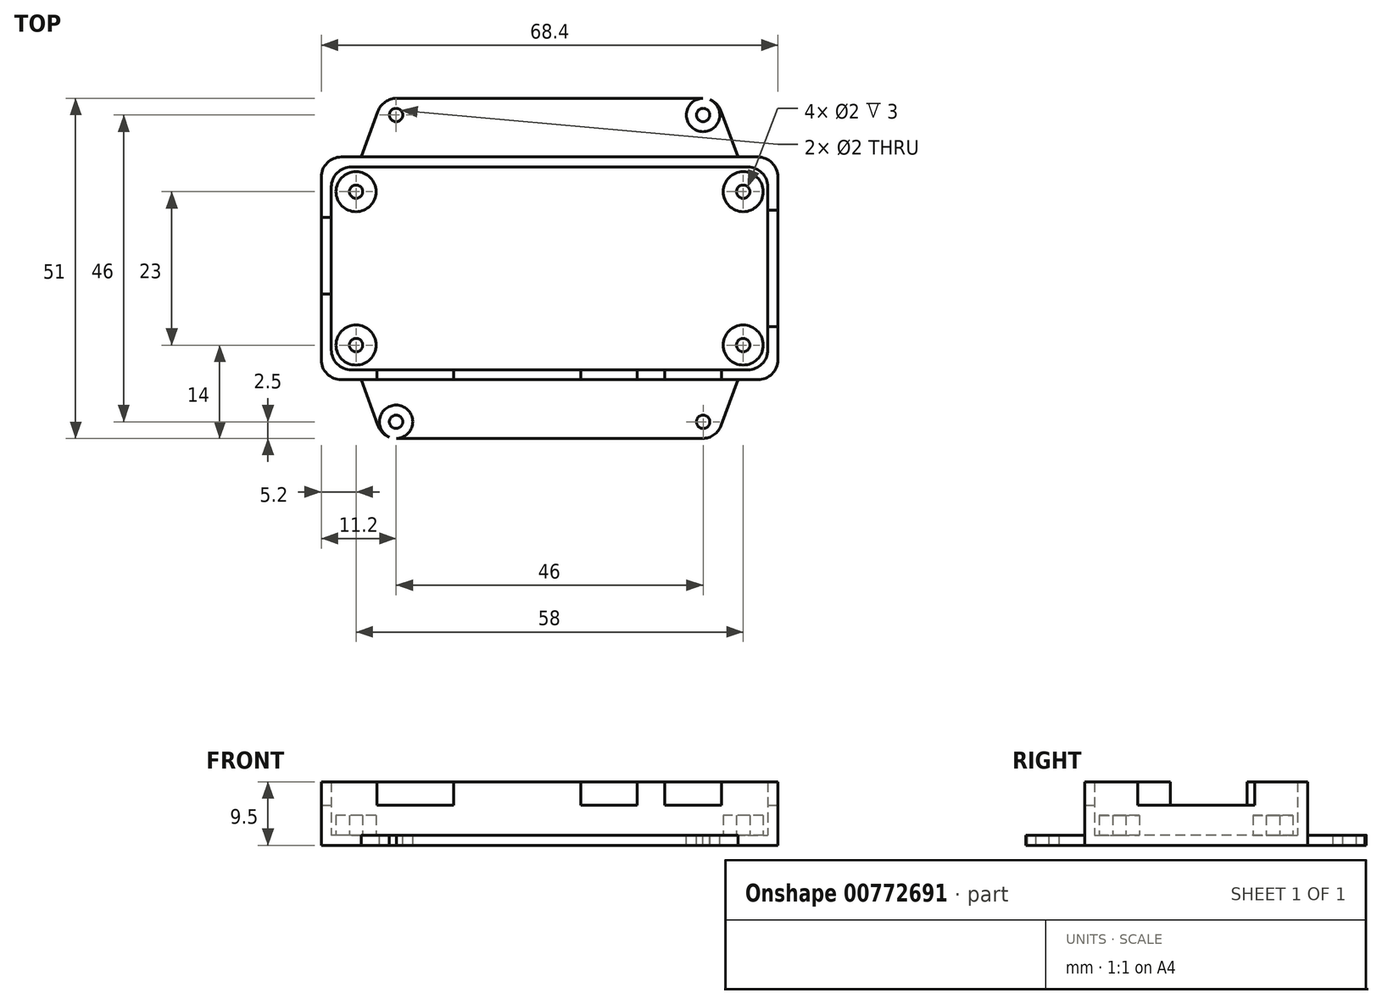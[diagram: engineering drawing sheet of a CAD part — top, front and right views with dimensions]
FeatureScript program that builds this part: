
annotation { "Feature Type Name" : "Feature", "Feature Type Description" : "" }
export const myFeature = defineFeature(function(context is Context, id is Id, definition is map)
    precondition{}
    {
        {
            var Q0;
            Q0=qCreatedBy(makeId("Top.planeOp"),FACE);
            var sketch = newSketch(context, id + "F0", { "sketchPlane" : qUnion([Q0])});
            skLineSegment(sketch, "E0", {"start": v(0, 31.79) * mm, "end": v(0, -34.92) * mm, "construction": true});
            skLineSegment(sketch, "E1", {"start": v(-57.68, 0) * mm, "end": v(57.82, 0) * mm, "construction": true});
            skLineSegment(sketch, "E2.bottom", {"start": v(-29.5, 15) * mm, "end": v(29.5, 15) * mm, "construction": true});
            skLineSegment(sketch, "E2.top", {"start": v(-29.5, -15) * mm, "end": v(29.5, -15) * mm, "construction": true});
            skLineSegment(sketch, "E2.left", {"start": v(-32.5, 12) * mm, "end": v(-32.5, -12) * mm, "construction": true});
            skLineSegment(sketch, "E2.right", {"start": v(32.5, 12) * mm, "end": v(32.5, -12) * mm, "construction": true});
            skPoint(sketch, "E3.visualSharp", {"position": v(-32.5, 15) * mm});
            skArc(sketch, "E3.filletArc", {"start": v(-29.5, 15) * mm, "mid": v(-31.62, 14.12) * mm, "end": v(-32.5, 12) * mm, "construction": true});
            skPoint(sketch, "E4.visualSharp", {"position": v(32.5, 15) * mm});
            skArc(sketch, "E4.filletArc", {"start": v(32.5, 12) * mm, "mid": v(31.62, 14.12) * mm, "end": v(29.5, 15) * mm, "construction": true});
            skPoint(sketch, "E5.visualSharp", {"position": v(32.5, -15) * mm});
            skArc(sketch, "E5.filletArc", {"start": v(29.5, -15) * mm, "mid": v(31.62, -14.12) * mm, "end": v(32.5, -12) * mm, "construction": true});
            skPoint(sketch, "E6.visualSharp", {"position": v(-32.5, -15) * mm});
            skArc(sketch, "E6.filletArc", {"start": v(-32.5, -12) * mm, "mid": v(-31.62, -14.12) * mm, "end": v(-29.5, -15) * mm, "construction": true});
            skCircle(sketch, "E7", {"center": v(-29, 11.5) * mm, "radius": 3 * mm});
            skCircle(sketch, "E8.0.1.0", {"center": v(-29, -11.5) * mm, "radius": 3 * mm});
            skCircle(sketch, "E8.1.0.0", {"center": v(29, 11.5) * mm, "radius": 3 * mm});
            skCircle(sketch, "E8.1.1.0", {"center": v(29, -11.5) * mm, "radius": 3 * mm});
            skLineSegment(sketch, "E8.direction1", {"start": v(-29, 11.5) * mm, "end": v(29, 11.5) * mm, "construction": true});
            skLineSegment(sketch, "E8.direction2", {"start": v(-29, 11.5) * mm, "end": v(-29, -11.5) * mm, "construction": true});
            skCircle(sketch, "E9", {"center": v(-29, 11.5) * mm, "radius": 1 * mm});
            skCircle(sketch, "E10.0.1.0", {"center": v(-29, -11.5) * mm, "radius": 1 * mm});
            skCircle(sketch, "E10.1.0.0", {"center": v(29, 11.5) * mm, "radius": 1 * mm});
            skCircle(sketch, "E10.1.1.0", {"center": v(29, -11.5) * mm, "radius": 1 * mm});
            skLineSegment(sketch, "E11.bottom", {"start": v(-29.7, 15.2) * mm, "end": v(29.7, 15.2) * mm});
            skLineSegment(sketch, "E11.top", {"start": v(-29.7, -15.2) * mm, "end": v(29.7, -15.2) * mm});
            skLineSegment(sketch, "E11.left", {"start": v(-32.7, 12.2) * mm, "end": v(-32.7, -12.2) * mm});
            skLineSegment(sketch, "E11.right", {"start": v(32.7, 12.2) * mm, "end": v(32.7, -12.2) * mm});
            skPoint(sketch, "E12.visualSharp", {"position": v(-32.7, 15.2) * mm});
            skArc(sketch, "E12.filletArc", {"start": v(-29.7, 15.2) * mm, "mid": v(-31.82, 14.32) * mm, "end": v(-32.7, 12.2) * mm});
            skPoint(sketch, "E13.visualSharp", {"position": v(-32.7, -15.2) * mm});
            skArc(sketch, "E13.filletArc", {"start": v(-32.7, -12.2) * mm, "mid": v(-31.82, -14.32) * mm, "end": v(-29.7, -15.2) * mm});
            skPoint(sketch, "E14.visualSharp", {"position": v(32.7, -15.2) * mm});
            skArc(sketch, "E14.filletArc", {"start": v(29.7, -15.2) * mm, "mid": v(31.82, -14.32) * mm, "end": v(32.7, -12.2) * mm});
            skPoint(sketch, "E15.visualSharp", {"position": v(32.7, 15.2) * mm});
            skArc(sketch, "E15.filletArc", {"start": v(32.7, 12.2) * mm, "mid": v(31.82, 14.32) * mm, "end": v(29.7, 15.2) * mm});
            skLineSegment(sketch, "E16.bottom", {"start": v(-31.2, 16.7) * mm, "end": v(31.2, 16.7) * mm});
            skLineSegment(sketch, "E16.top", {"start": v(-31.2, -16.7) * mm, "end": v(31.2, -16.7) * mm});
            skLineSegment(sketch, "E16.left", {"start": v(-34.2, 13.7) * mm, "end": v(-34.2, -13.7) * mm});
            skLineSegment(sketch, "E16.right", {"start": v(34.2, 13.7) * mm, "end": v(34.2, -13.7) * mm});
            skPoint(sketch, "E17.visualSharp", {"position": v(-34.2, 16.7) * mm});
            skArc(sketch, "E17.filletArc", {"start": v(-31.2, 16.7) * mm, "mid": v(-33.32, 15.82) * mm, "end": v(-34.2, 13.7) * mm});
            skPoint(sketch, "E18.visualSharp", {"position": v(-34.2, -16.7) * mm});
            skArc(sketch, "E18.filletArc", {"start": v(-34.2, -13.7) * mm, "mid": v(-33.32, -15.82) * mm, "end": v(-31.2, -16.7) * mm});
            skPoint(sketch, "E19.visualSharp", {"position": v(34.2, -16.7) * mm});
            skArc(sketch, "E19.filletArc", {"start": v(31.2, -16.7) * mm, "mid": v(33.32, -15.82) * mm, "end": v(34.2, -13.7) * mm});
            skPoint(sketch, "E20.visualSharp", {"position": v(34.2, 16.7) * mm});
            skArc(sketch, "E20.filletArc", {"start": v(34.2, 13.7) * mm, "mid": v(33.32, 15.82) * mm, "end": v(31.2, 16.7) * mm});
            skLineSegment(sketch, "E21", {"start": v(-36.24, 1.9) * mm, "end": v(-30.97, 1.9) * mm, "construction": true});
            skLineSegment(sketch, "E22", {"start": v(-20.1, -13.64) * mm, "end": v(-20.1, -19.07) * mm, "construction": true});
            skLineSegment(sketch, "E23", {"start": v(8.9, -12.93) * mm, "end": v(8.9, -18.66) * mm, "construction": true});
            skLineSegment(sketch, "E24", {"start": v(21.5, -12.58) * mm, "end": v(21.5, -18.71) * mm, "construction": true});
            skLineSegment(sketch, "E25", {"start": v(-25.85, -16.7) * mm, "end": v(-25.85, -15.2) * mm});
            skLineSegment(sketch, "E26", {"start": v(-14.35, -16.7) * mm, "end": v(-14.35, -15.2) * mm});
            skLineSegment(sketch, "E27", {"start": v(4.65, -16.7) * mm, "end": v(4.65, -15.2) * mm});
            skLineSegment(sketch, "E28", {"start": v(13.15, -15.2) * mm, "end": v(13.15, -16.7) * mm});
            skLineSegment(sketch, "E29", {"start": v(17.25, -16.7) * mm, "end": v(17.25, -15.2) * mm});
            skLineSegment(sketch, "E30", {"start": v(25.75, -15.2) * mm, "end": v(25.75, -16.7) * mm});
            skLineSegment(sketch, "E31", {"start": v(-34.2, 7.65) * mm, "end": v(-32.7, 7.65) * mm});
            skLineSegment(sketch, "E32", {"start": v(-34.2, -3.85) * mm, "end": v(-32.7, -3.85) * mm});
            skLineSegment(sketch, "E33", {"start": v(32.7, 8.75) * mm, "end": v(34.2, 8.75) * mm});
            skLineSegment(sketch, "E34", {"start": v(32.7, -8.75) * mm, "end": v(34.2, -8.75) * mm});
            skSolve(sketch);
        }
        {
            var Q0;
            Q0 = qSketchRegion(id + "F0", true);
            var Q1;
            Q1=makeQuery(id+"F0.imprint","IMPRINT",FACE,{"disambiguationData":[TD([[makeQuery(id+"F0.imprint","IMPRINT",EDGE,{"derivedFrom":sQuery(id+"F0.wireOp",EDGE,"E7")}),-1.0]])]});
            var Q2;
            Q2=makeQuery(id+"F0.imprint","IMPRINT",FACE,{"disambiguationData":[TD([[makeQuery(id+"F0.imprint","IMPRINT",EDGE,{"derivedFrom":sQuery(id+"F0.wireOp",EDGE,"E10.0.1.0")}),1.0]])]});
            var Q3;
            Q3=makeQuery(id+"F0.imprint","IMPRINT",FACE,{"disambiguationData":[TD([[makeQuery(id+"F0.imprint","IMPRINT",EDGE,{"derivedFrom":sQuery(id+"F0.wireOp",EDGE,"E8.0.1.0")}),1.0]])]});
            var Q4;
            Q4=makeQuery(id+"F0.imprint","IMPRINT",FACE,{"disambiguationData":[TD([[makeQuery(id+"F0.imprint","IMPRINT",EDGE,{"derivedFrom":sQuery(id+"F0.wireOp",EDGE,"E9")}),1.0]])]});
            var Q5;
            Q5=makeQuery(id+"F0.imprint","IMPRINT",FACE,{"disambiguationData":[TD([[makeQuery(id+"F0.imprint","IMPRINT",EDGE,{"derivedFrom":sQuery(id+"F0.wireOp",EDGE,"E7")}),1.0]])]});
            var Q6;
            Q6=makeQuery(id+"F0.imprint","IMPRINT",FACE,{"disambiguationData":[TD([[makeQuery(id+"F0.imprint","IMPRINT",EDGE,{"derivedFrom":sQuery(id+"F0.wireOp",EDGE,"E10.1.1.0")}),1.0]])]});
            var Q7;
            Q7=makeQuery(id+"F0.imprint","IMPRINT",FACE,{"disambiguationData":[TD([[makeQuery(id+"F0.imprint","IMPRINT",EDGE,{"derivedFrom":sQuery(id+"F0.wireOp",EDGE,"E8.1.1.0")}),1.0]])]});
            var Q8;
            Q8=makeQuery(id+"F0.imprint","IMPRINT",FACE,{"disambiguationData":[TD([[makeQuery(id+"F0.imprint","IMPRINT",EDGE,{"derivedFrom":sQuery(id+"F0.wireOp",EDGE,"E10.1.0.0")}),1.0]])]});
            var Q9;
            Q9=makeQuery(id+"F0.imprint","IMPRINT",FACE,{"disambiguationData":[TD([[makeQuery(id+"F0.imprint","IMPRINT",EDGE,{"derivedFrom":sQuery(id+"F0.wireOp",EDGE,"E8.1.0.0")}),1.0]])]});
            extrude(context, id + "F1", {"entities" : qUnion([Q0, Q1, Q2, Q3, Q4, Q5, Q6, Q7, Q8, Q9]), "oppositeDirection" : true, "depth" : 1.5 * mm, "offsetDistance" : 25 * mm});
        }
        {
            var Q0;
            Q0=makeQuery(id+"F0.imprint","IMPRINT",FACE,{"disambiguationData":[TD([[makeQuery(id+"F0.imprint","IMPRINT",EDGE,{"derivedFrom":sQuery(id+"F0.wireOp",EDGE,"E7")}),1.0]])]});
            var Q1;
            Q1=makeQuery(id+"F0.imprint","IMPRINT",FACE,{"disambiguationData":[TD([[makeQuery(id+"F0.imprint","IMPRINT",EDGE,{"derivedFrom":sQuery(id+"F0.wireOp",EDGE,"E8.0.1.0")}),1.0]])]});
            var Q2;
            Q2=makeQuery(id+"F0.imprint","IMPRINT",FACE,{"disambiguationData":[TD([[makeQuery(id+"F0.imprint","IMPRINT",EDGE,{"derivedFrom":sQuery(id+"F0.wireOp",EDGE,"E8.1.0.0")}),1.0]])]});
            var Q3;
            Q3=makeQuery(id+"F0.imprint","IMPRINT",FACE,{"disambiguationData":[TD([[makeQuery(id+"F0.imprint","IMPRINT",EDGE,{"derivedFrom":sQuery(id+"F0.wireOp",EDGE,"E8.1.1.0")}),1.0]])]});
            extrude(context, id + "F2", {"entities" : qUnion([Q0, Q1, Q2, Q3]), "operationType" : NewBodyOperationType.ADD, "depth" : 3 * mm, "offsetDistance" : 25 * mm});
        }
        {
            var Q0;
            {var subQ3=sQuery(id+"F0.wireOp",EDGE,"E13.filletArc");Q0=makeQuery(id+"F0.imprint","IMPRINT",FACE,{"disambiguationData":[TD([[makeQuery(id+"F0.imprint","IMPRINT",EDGE,{"derivedFrom":subQ3}),-1.0]])]});}
            var Q1;
            Q1=makeQuery(id+"F0.imprint","IMPRINT",FACE,{"disambiguationData":[TD([[makeQuery(id+"F0.imprint","IMPRINT",EDGE,{"derivedFrom":sQuery(id+"F0.wireOp",EDGE,"E11.bottom")}),1.0]])]});
            var Q2;
            {var subQ0=sQuery(id+"F0.wireOp",EDGE,"E26");Q2=makeQuery(id+"F0.imprint","IMPRINT",FACE,{"disambiguationData":[TD([[makeQuery(id+"F0.imprint","IMPRINT",EDGE,{"derivedFrom":subQ0}),-1.0]])]});}
            var Q3;
            {var subQ0=sQuery(id+"F0.wireOp",EDGE,"E28");Q3=makeQuery(id+"F0.imprint","IMPRINT",FACE,{"disambiguationData":[TD([[makeQuery(id+"F0.imprint","IMPRINT",EDGE,{"derivedFrom":subQ0}),1.0]])]});}
            var Q4;
            {var subQ3=sQuery(id+"F0.wireOp",EDGE,"E14.filletArc");Q4=makeQuery(id+"F0.imprint","IMPRINT",FACE,{"disambiguationData":[TD([[makeQuery(id+"F0.imprint","IMPRINT",EDGE,{"derivedFrom":subQ3}),-1.0]])]});}
            extrude(context, id + "F3", {"entities" : qUnion([Q0, Q1, Q2, Q3, Q4]), "operationType" : NewBodyOperationType.ADD, "depth" : 8 * mm, "offsetDistance" : 25 * mm});
        }
        {
            var Q0;
            {var subQ0=sQuery(id+"F0.wireOp",EDGE,"E31");Q0=makeQuery(id+"F0.imprint","IMPRINT",FACE,{"disambiguationData":[TD([[makeQuery(id+"F0.imprint","IMPRINT",EDGE,{"derivedFrom":subQ0}),-1.0]])]});}
            var Q1;
            {var subQ0=sQuery(id+"F0.wireOp",EDGE,"E25");Q1=makeQuery(id+"F0.imprint","IMPRINT",FACE,{"disambiguationData":[TD([[makeQuery(id+"F0.imprint","IMPRINT",EDGE,{"derivedFrom":subQ0}),-1.0]])]});}
            var Q2;
            {var subQ0=sQuery(id+"F0.wireOp",EDGE,"E27");Q2=makeQuery(id+"F0.imprint","IMPRINT",FACE,{"disambiguationData":[TD([[makeQuery(id+"F0.imprint","IMPRINT",EDGE,{"derivedFrom":subQ0}),-1.0]])]});}
            var Q3;
            {var subQ0=sQuery(id+"F0.wireOp",EDGE,"E29");Q3=makeQuery(id+"F0.imprint","IMPRINT",FACE,{"disambiguationData":[TD([[makeQuery(id+"F0.imprint","IMPRINT",EDGE,{"derivedFrom":subQ0}),-1.0]])]});}
            var Q4;
            {var subQ0=sQuery(id+"F0.wireOp",EDGE,"E33");Q4=makeQuery(id+"F0.imprint","IMPRINT",FACE,{"disambiguationData":[TD([[makeQuery(id+"F0.imprint","IMPRINT",EDGE,{"derivedFrom":subQ0}),-1.0]])]});}
            extrude(context, id + "F4", {"entities" : qUnion([Q0, Q1, Q2, Q3, Q4]), "operationType" : NewBodyOperationType.ADD, "depth" : 4.5 * mm, "offsetDistance" : 25 * mm});
        }
        {
            var Q0;
            Q0=qCreatedBy(makeId("Top.planeOp"),FACE);
            var sketch = newSketch(context, id + "F5", { "sketchPlane" : qUnion([Q0])});
            skLineSegment(sketch, "E35.0", {"start": v(-31.2, 16.7) * mm, "end": v(31.2, 16.7) * mm, "construction": true});
            skLineSegment(sketch, "E36", {"start": v(-28.2, 16.7) * mm, "end": v(-25.72, 23.53) * mm});
            skLineSegment(sketch, "E37", {"start": v(-22.9, 25.5) * mm, "end": v(22.9, 25.5) * mm});
            skLineSegment(sketch, "E38", {"start": v(25.72, 23.53) * mm, "end": v(28.2, 16.7) * mm});
            skLineSegment(sketch, "E39.0", {"start": v(-31.2, -16.7) * mm, "end": v(31.2, -16.7) * mm, "construction": true});
            skLineSegment(sketch, "E40", {"start": v(-28.2, -16.7) * mm, "end": v(-25.72, -23.53) * mm});
            skLineSegment(sketch, "E41", {"start": v(-22.9, -25.5) * mm, "end": v(22.9, -25.5) * mm});
            skLineSegment(sketch, "E42", {"start": v(25.72, -23.53) * mm, "end": v(28.2, -16.7) * mm});
            skPoint(sketch, "E43.visualSharp", {"position": v(-25, -25.5) * mm});
            skArc(sketch, "E43.filletArc", {"start": v(-25.72, -23.53) * mm, "mid": v(-24.62, -24.96) * mm, "end": v(-22.9, -25.5) * mm});
            skPoint(sketch, "E44.visualSharp", {"position": v(25, -25.5) * mm});
            skArc(sketch, "E44.filletArc", {"start": v(22.9, -25.5) * mm, "mid": v(24.62, -24.96) * mm, "end": v(25.72, -23.53) * mm});
            skPoint(sketch, "E45.visualSharp", {"position": v(25, 25.5) * mm});
            skArc(sketch, "E45.filletArc", {"start": v(25.72, 23.53) * mm, "mid": v(24.62, 24.96) * mm, "end": v(22.9, 25.5) * mm});
            skPoint(sketch, "E46.visualSharp", {"position": v(-25, 25.5) * mm});
            skArc(sketch, "E46.filletArc", {"start": v(-22.9, 25.5) * mm, "mid": v(-24.62, 24.96) * mm, "end": v(-25.72, 23.53) * mm});
            skLineSegment(sketch, "E47", {"start": v(-28.2, 16.7) * mm, "end": v(28.2, 16.7) * mm});
            skLineSegment(sketch, "E48", {"start": v(-28.2, -16.7) * mm, "end": v(28.2, -16.7) * mm});
            skCircle(sketch, "E49", {"center": v(-23, 23) * mm, "radius": 2.5 * mm});
            skCircle(sketch, "E50.MirrorC", {"center": v(23, 23) * mm, "radius": 2.5 * mm});
            skCircle(sketch, "E51.MirrorC", {"center": v(-23, -23) * mm, "radius": 2.5 * mm});
            skCircle(sketch, "E52.MirrorC", {"center": v(23, -23) * mm, "radius": 2.5 * mm});
            skCircle(sketch, "E53", {"center": v(-23, 23) * mm, "radius": 1 * mm});
            skCircle(sketch, "E54.MirrorC", {"center": v(23, 23) * mm, "radius": 1 * mm});
            skCircle(sketch, "E55.MirrorC", {"center": v(-23, -23) * mm, "radius": 1 * mm});
            skCircle(sketch, "E56.MirrorC", {"center": v(23, -23) * mm, "radius": 1 * mm});
            skSolve(sketch);
        }
        {
            var Q0;
            {var subQ1=sQuery(id+"F5.wireOp",EDGE,"E40");Q0=makeQuery(id+"F5.imprint","IMPRINT",FACE,{"disambiguationData":[TD([[makeQuery(id+"F5.imprint","IMPRINT",EDGE,{"derivedFrom":subQ1}),1.0]])]});}
            var Q1;
            Q1=makeQuery(id+"F5.imprint","IMPRINT",FACE,{"disambiguationData":[TD([[makeQuery(id+"F5.imprint","IMPRINT",EDGE,{"derivedFrom":sQuery(id+"F5.wireOp",EDGE,"E55.MirrorC")}),1.0]])]});
            var Q2;
            Q2=makeQuery(id+"F5.imprint","IMPRINT",FACE,{"disambiguationData":[TD([[makeQuery(id+"F5.imprint","IMPRINT",EDGE,{"derivedFrom":sQuery(id+"F5.wireOp",EDGE,"E56.MirrorC")}),-1.0]])]});
            var Q3;
            {var subQ6=sQuery(id+"F5.wireOp",EDGE,"E36");Q3=makeQuery(id+"F5.imprint","IMPRINT",FACE,{"disambiguationData":[TD([[makeQuery(id+"F5.imprint","IMPRINT",EDGE,{"derivedFrom":subQ6}),-1.0]])]});}
            var Q4;
            Q4=makeQuery(id+"F5.imprint","IMPRINT",FACE,{"disambiguationData":[TD([[makeQuery(id+"F5.imprint","IMPRINT",EDGE,{"derivedFrom":sQuery(id+"F5.wireOp",EDGE,"E53")}),-1.0]])]});
            var Q5;
            Q5=makeQuery(id+"F5.imprint","IMPRINT",FACE,{"disambiguationData":[TD([[makeQuery(id+"F5.imprint","IMPRINT",EDGE,{"derivedFrom":sQuery(id+"F5.wireOp",EDGE,"E54.MirrorC")}),1.0]])]});
            extrude(context, id + "F6", {"entities" : qUnion([Q0, Q1, Q2, Q3, Q4, Q5]), "operationType" : NewBodyOperationType.ADD, "oppositeDirection" : true, "depth" : 1.5 * mm, "offsetDistance" : 25 * mm});
        }
    });
